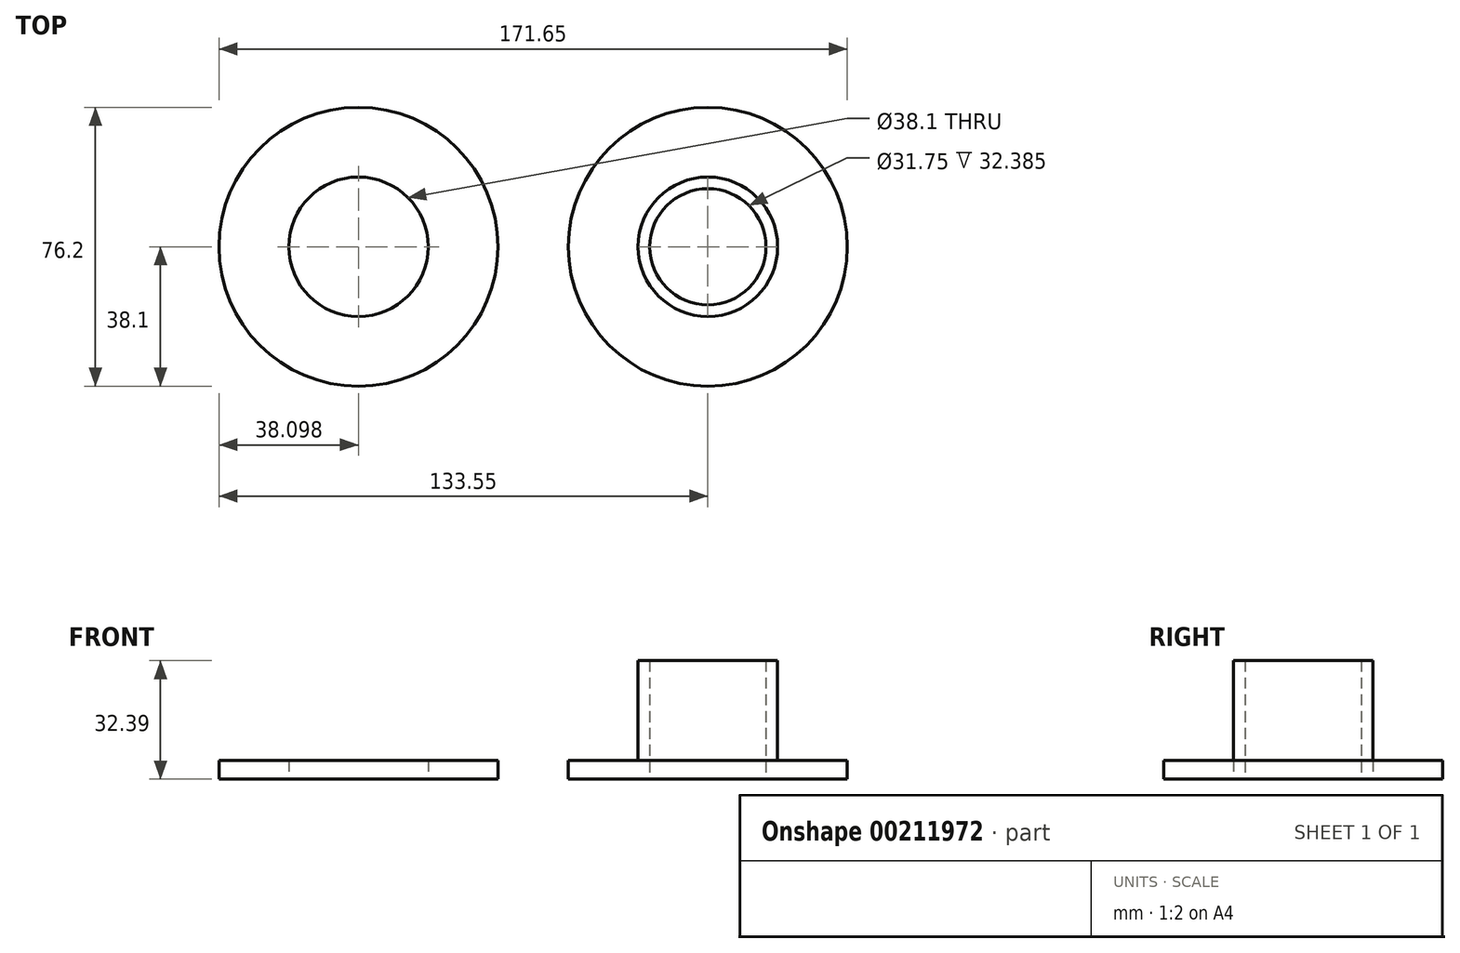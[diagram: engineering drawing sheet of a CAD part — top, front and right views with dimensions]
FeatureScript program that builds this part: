
annotation { "Feature Type Name" : "Feature", "Feature Type Description" : "" }
export const myFeature = defineFeature(function(context is Context, id is Id, definition is map)
    precondition{}
    {
        {
            var Q0;
            Q0=qCreatedBy(makeId("Top.planeOp"),FACE);
            var sketch = newSketch(context, id + "F0", { "sketchPlane" : qUnion([Q0])});
            skCircle(sketch, "E0", {"center": v(-61.41, 0) * mm, "radius": 38.1 * mm});
            skCircle(sketch, "E1", {"center": v(34.04, 0) * mm, "radius": 38.1 * mm});
            skCircle(sketch, "E2", {"center": v(34.04, 0) * mm, "radius": 15.88 * mm});
            skCircle(sketch, "E3", {"center": v(34.04, 0) * mm, "radius": 19.05 * mm});
            skCircle(sketch, "E4", {"center": v(-61.41, 0) * mm, "radius": 19.05 * mm});
            skSolve(sketch);
        }
        {
            var Q0;
            Q0=makeQuery(id+"F0.imprint","IMPRINT",FACE,{"disambiguationData":[TD([[makeQuery(id+"F0.imprint","IMPRINT",EDGE,{"derivedFrom":sQuery(id+"F0.wireOp",EDGE,"E1")}),1.0]])]});
            var Q1;
            Q1=makeQuery(id+"F0.imprint","IMPRINT",FACE,{"disambiguationData":[TD([[makeQuery(id+"F0.imprint","IMPRINT",EDGE,{"derivedFrom":sQuery(id+"F0.wireOp",EDGE,"E0")}),1.0]])]});
            extrude(context, id + "F1", {"entities" : qUnion([Q0, Q1]), "depth" : 5.08 * mm});
        }
        {
            var Q0;
            Q0=makeQuery(id+"F0.imprint","IMPRINT",FACE,{"disambiguationData":[TD([[makeQuery(id+"F0.imprint","IMPRINT",EDGE,{"derivedFrom":sQuery(id+"F0.wireOp",EDGE,"E2")}),-1.0]])]});
            extrude(context, id + "F2", {"entities" : qUnion([Q0]), "operationType" : NewBodyOperationType.ADD, "depth" : 32.38 * mm});
        }
    });
